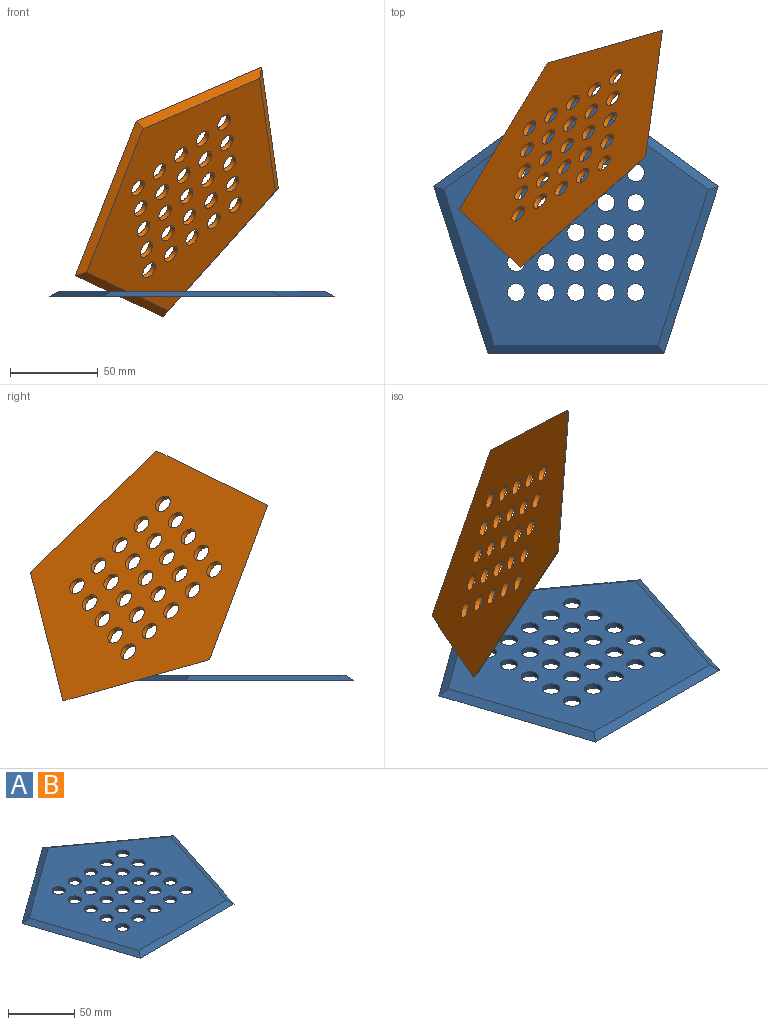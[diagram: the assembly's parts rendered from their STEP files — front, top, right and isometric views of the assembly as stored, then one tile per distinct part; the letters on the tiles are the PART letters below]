
ASSEMBLY  parts=2 mates=1
PART A: 32 faces, bbox 161.8x153.9x3 mm
  f0: plane 95.11x34.43mm, normal (-0.5,-0.16,0.85), area 550.5mm2, adj f1,f4,f5,f6
  f1: plane 100x4.85mm, normal (0,-0.53,0.85), area 550.5mm2, adj f0,f2,f5,f6
  f2: plane 95.11x34.43mm, normal (0.5,-0.16,0.85), area 550.5mm2, adj f1,f3,f5,f6
  f3: plane 80.9x60.63mm, normal (0.31,0.43,0.85), area 550.5mm2, adj f2,f4,f5,f6
  f4: plane 80.9x60.63mm, normal (-0.31,0.43,0.85), area 550.5mm2, adj f0,f3,f5,f6
  f5: plane 150.39x143.03mm, normal (0,0,1), area 12899.8mm2, adj f0,f1,f2,f3,f4,f7,f8,f9
  f6: plane 161.8x153.88mm, normal (0,0,-1), area 15241.3mm2, adj f0,f1,f2,f3,f4,f7,f8,f9
  f7: cylinder r=5mm len=10mm, axis (0,0,1), area 94.2mm2, adj f5,f6
  f8: cylinder r=5mm len=10mm, axis (0,0,1), area 94.2mm2, adj f5,f6
  f9: cylinder r=5mm len=10mm, axis (0,0,1), area 94.2mm2, adj f5,f6
  f10: cylinder r=5mm len=10mm, axis (0,0,1), area 94.2mm2, adj f5,f6
  f11: cylinder r=5mm len=10mm, axis (0,0,1), area 94.2mm2, adj f5,f6
  f12: cylinder r=5mm len=10mm, axis (0,0,1), area 94.2mm2, adj f5,f6
  f13: cylinder r=5mm len=10mm, axis (0,0,1), area 94.2mm2, adj f5,f6
  f14: cylinder r=5mm len=10mm, axis (0,0,1), area 94.2mm2, adj f5,f6
  f15: cylinder r=5mm len=10mm, axis (0,0,1), area 94.2mm2, adj f5,f6
  f16: cylinder r=5mm len=10mm, axis (0,0,1), area 94.2mm2, adj f5,f6
  f17: cylinder r=5mm len=10mm, axis (0,0,1), area 94.2mm2, adj f5,f6
  f18: cylinder r=5mm len=10mm, axis (0,0,1), area 94.2mm2, adj f5,f6
  f19: cylinder r=5mm len=10mm, axis (0,0,1), area 94.2mm2, adj f5,f6
  f20: cylinder r=5mm len=10mm, axis (0,0,1), area 94.2mm2, adj f5,f6
  f21: cylinder r=5mm len=10mm, axis (0,0,1), area 94.2mm2, adj f5,f6
  f22: cylinder r=5mm len=10mm, axis (0,0,1), area 94.2mm2, adj f5,f6
  f23: cylinder r=5mm len=10mm, axis (0,0,1), area 94.2mm2, adj f5,f6
  f24: cylinder r=5mm len=10mm, axis (0,0,1), area 94.2mm2, adj f5,f6
  f25: cylinder r=5mm len=10mm, axis (0,0,1), area 94.2mm2, adj f5,f6
  f26: cylinder r=5mm len=10mm, axis (0,0,1), area 94.2mm2, adj f5,f6
  f27: cylinder r=5mm len=10mm, axis (0,0,1), area 94.2mm2, adj f5,f6
  f28: cylinder r=5mm len=10mm, axis (0,0,1), area 94.2mm2, adj f5,f6
  f29: cylinder r=5mm len=10mm, axis (0,0,1), area 94.2mm2, adj f5,f6
  f30: cylinder r=5mm len=10mm, axis (0,0,1), area 94.2mm2, adj f5,f6
  f31: cylinder r=5mm len=10mm, axis (0,0,1), area 94.2mm2, adj f5,f6
PART B: same geometry as A
PLACE A t=(18.75,6.15,112.67)mm fixed
PLACE B rot(axis=(0.67,-0.53,0.51),180deg) t=(13.61,55.63,171.14)mm
MATE planar A.f4 <-> B.f4  axis (-0.31,0.43,0.85) through (-20.29,59.89,114.16)mm
